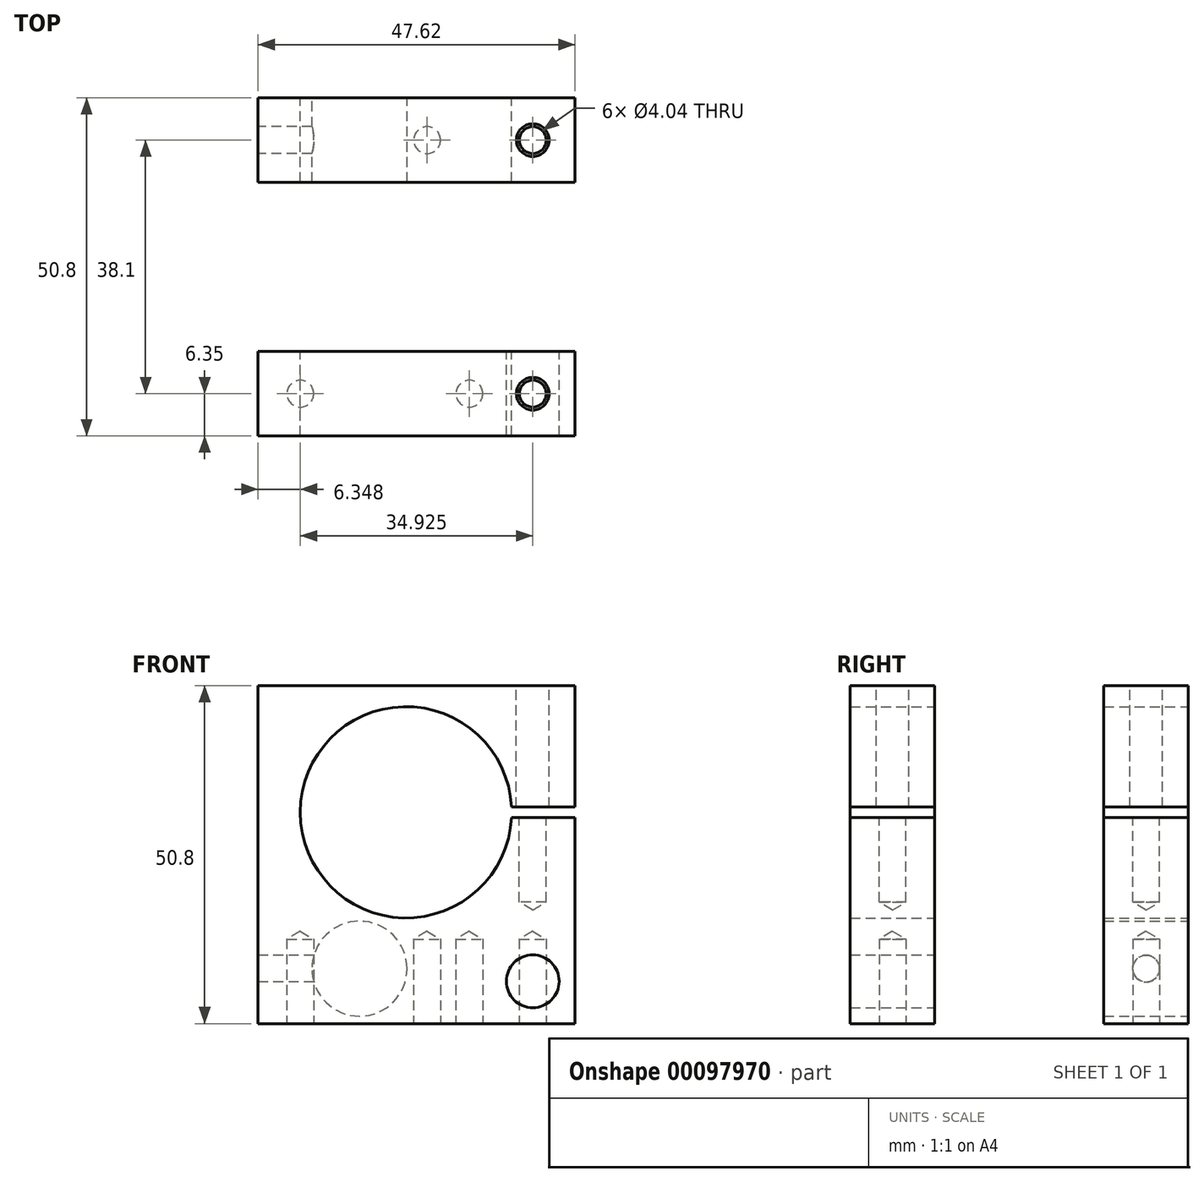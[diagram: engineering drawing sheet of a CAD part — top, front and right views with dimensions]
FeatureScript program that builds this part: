
annotation { "Feature Type Name" : "Feature", "Feature Type Description" : "" }
export const myFeature = defineFeature(function(context is Context, id is Id, definition is map)
    precondition{}
    {
        {
            var Q0;
            Q0=qCreatedBy(makeId("Front.planeOp"),FACE);
            var sketch = newSketch(context, id + "F0", { "sketchPlane" : qUnion([Q0])});
            skLineSegment(sketch, "E0.bottom", {"start": v(23.81, -25.4) * mm, "end": v(-23.81, -25.4) * mm});
            skLineSegment(sketch, "E0.top", {"start": v(23.81, 25.4) * mm, "end": v(-23.81, 25.4) * mm});
            skLineSegment(sketch, "E0.left", {"start": v(23.81, -25.4) * mm, "end": v(23.81, 25.4) * mm});
            skLineSegment(sketch, "E0.right", {"start": v(-23.81, -25.4) * mm, "end": v(-23.81, 25.4) * mm});
            skPoint(sketch, "E0.middle", {"position": v(0, 0) * mm});
            skLineSegment(sketch, "E1", {"start": v(-1.59, 25.4) * mm, "end": v(-1.59, -25.4) * mm, "construction": true});
            skLineSegment(sketch, "E2", {"start": v(-23.81, 6.35) * mm, "end": v(23.81, 6.35) * mm, "construction": true});
            skArc(sketch, "E3", {"start": v(14.27, 7.14) * mm, "mid": v(-17.46, 6.35) * mm, "end": v(14.27, 5.56) * mm});
            skLineSegment(sketch, "E4", {"start": v(-23.81, -17.15) * mm, "end": v(23.81, -17.14) * mm, "construction": true});
            skLineSegment(sketch, "E5", {"start": v(-8.57, -17.15) * mm, "end": v(-8.57, -25.4) * mm, "construction": true});
            skCircle(sketch, "E6", {"center": v(-8.57, -17.15) * mm, "radius": 7.14 * mm});
            skLineSegment(sketch, "E7", {"start": v(-23.81, 7.14) * mm, "end": v(23.81, 7.14) * mm, "construction": true});
            skLineSegment(sketch, "E8", {"start": v(-23.81, 5.56) * mm, "end": v(23.81, 5.56) * mm, "construction": true});
            skLineSegment(sketch, "E9", {"start": v(14.27, 7.14) * mm, "end": v(23.81, 7.14) * mm});
            skLineSegment(sketch, "E10", {"start": v(14.27, 5.56) * mm, "end": v(23.81, 5.56) * mm});
            skSolve(sketch);
        }
        {
            var Q0;
            {var subQ3=sQuery(id+"F0.wireOp",EDGE,"E0.bottom");Q0=makeQuery(id+"F0.imprint","IMPRINT",FACE,{"disambiguationData":[TD([[makeQuery(id+"F0.imprint","IMPRINT",EDGE,{"derivedFrom":subQ3}),-1.0]])]});}
            extrude(context, id + "F1", {"entities" : qUnion([Q0]), "depth" : 12.7 * mm});
        }
        {
            var Q0;
            Q0=makeQuery(id+"F1.opExtrude","SWEPT_FACE",FACE,{"disambiguationData":[OSD([sQuery(id+"F0.wireOp",EDGE,"E0.right")])]});
            var sketch = newSketch(context, id + "F2", { "sketchPlane" : qUnion([Q0])});
            skLineSegment(sketch, "E11.0.0", {"start": v(0, 25.4) * mm, "end": v(0, -25.4) * mm});
            skLineSegment(sketch, "E11.0.1", {"start": v(0, -25.4) * mm, "end": v(12.7, -25.4) * mm});
            skLineSegment(sketch, "E11.0.2", {"start": v(12.7, -25.4) * mm, "end": v(12.7, 25.4) * mm});
            skLineSegment(sketch, "E11.0.3", {"start": v(12.7, 25.4) * mm, "end": v(0, 25.4) * mm});
            skPoint(sketch, "E12.0", {"position": v(0, -17.14) * mm});
            skLineSegment(sketch, "E13", {"start": v(0, -17.14) * mm, "end": v(12.7, -17.14) * mm, "construction": true});
            skPoint(sketch, "E14", {"position": v(6.35, -17.14) * mm});
            skSolve(sketch);
        }
        {
            var Q0;
            Q0=sQuery(id+"F2.wireOp",VERTEX,"E14");
            var Q1;
            Q1=makeQuery(id+"F1.opExtrude","SWEPT_BODY",BODY,{"disambiguationData":[OSD([sQuery(id+"F0.wireOp",EDGE,"E0.bottom"),sQuery(id+"F0.wireOp",EDGE,"E0.top"),sQuery(id+"F0.wireOp",EDGE,"E0.left"),sQuery(id+"F0.wireOp",EDGE,"E0.right"),sQuery(id+"F0.wireOp",EDGE,"E3"),sQuery(id+"F0.wireOp",EDGE,"E6"),sQuery(id+"F0.wireOp",EDGE,"E9"),sQuery(id+"F0.wireOp",EDGE,"E10")])]});
            hole(context, id + "F3", {"style" : HoleStyle.SIMPLE, "endStyle" : HoleEndStyle.BLIND, "standardTappedOrClearance" : lookupTablePath({ "standard" : "ANSI", "engagement" : "75%", "pitch" : "32 tpi", "size" : "#10", "type" : "Tapped" }), "standardBlindInLast" : lookupTablePath({ "standard" : "ANSI", "engagement" : "75%", "pitch" : "32 tpi", "size" : "#10", "type" : "Tapped" }), "holeDiameter" : 4.04 * mm, "holeDepth" : 9.52 * mm, "locations" : qUnion([Q0]), "scope" : qUnion([Q1]), "majorDiameter" : 4.83 * mm});
        }
        {
            var Q0;
            Q0=makeQuery(id+"F1.opExtrude","SWEPT_FACE",FACE,{"disambiguationData":[OSD([sQuery(id+"F0.wireOp",EDGE,"E0.bottom")])]});
            var sketch = newSketch(context, id + "F4", { "sketchPlane" : qUnion([Q0])});
            skLineSegment(sketch, "E15", {"start": v(17.46, 12.7) * mm, "end": v(17.46, 0) * mm, "construction": true});
            skLineSegment(sketch, "E16", {"start": v(1.59, 12.7) * mm, "end": v(1.59, 0) * mm, "construction": true});
            skPoint(sketch, "E17", {"position": v(1.59, 6.35) * mm});
            skPoint(sketch, "E18", {"position": v(17.46, 6.35) * mm});
            skSolve(sketch);
        }
        {
            var Q0;
            Q0=sQuery(id+"F4.wireOp",VERTEX,"E17");
            var Q1;
            Q1=sQuery(id+"F4.wireOp",VERTEX,"E18");
            var Q2;
            Q2=makeQuery(id+"F1.opExtrude","SWEPT_BODY",BODY,{"disambiguationData":[OSD([sQuery(id+"F0.wireOp",EDGE,"E0.bottom"),sQuery(id+"F0.wireOp",EDGE,"E0.top"),sQuery(id+"F0.wireOp",EDGE,"E0.left"),sQuery(id+"F0.wireOp",EDGE,"E0.right"),sQuery(id+"F0.wireOp",EDGE,"E3"),sQuery(id+"F0.wireOp",EDGE,"E6"),sQuery(id+"F0.wireOp",EDGE,"E9"),sQuery(id+"F0.wireOp",EDGE,"E10")])]});
            hole(context, id + "F5", {"style" : HoleStyle.SIMPLE, "endStyle" : HoleEndStyle.BLIND, "standardTappedOrClearance" : lookupTablePath({ "standard" : "ANSI", "engagement" : "75%", "pitch" : "32 tpi", "size" : "#10", "type" : "Tapped" }), "standardBlindInLast" : lookupTablePath({ "standard" : "ANSI", "engagement" : "75%", "pitch" : "32 tpi", "size" : "#10", "type" : "Tapped" }), "holeDiameter" : 4.04 * mm, "holeDepth" : 12.7 * mm, "locations" : qUnion([Q0, Q1]), "scope" : qUnion([Q2]), "majorDiameter" : 4.83 * mm});
        }
        {
            var Q0;
            Q0=makeQuery(id+"F1.opExtrude","SWEPT_FACE",FACE,{"disambiguationData":[OSD([sQuery(id+"F0.wireOp",EDGE,"E10")])]});
            var sketch = newSketch(context, id + "F6", { "sketchPlane" : qUnion([Q0])});
            skLineSegment(sketch, "E19.0", {"start": v(14.27, -12.7) * mm, "end": v(23.81, -12.7) * mm, "construction": true});
            skLineSegment(sketch, "E20.0", {"start": v(23.81, -12.7) * mm, "end": v(23.81, 0) * mm, "construction": true});
            skLineSegment(sketch, "E21", {"start": v(17.46, 0) * mm, "end": v(17.46, -12.7) * mm, "construction": true});
            skPoint(sketch, "E22", {"position": v(17.46, -6.35) * mm});
            skSolve(sketch);
        }
        {
            var Q0;
            Q0=sQuery(id+"F6.wireOp",VERTEX,"E22");
            var Q1;
            Q1=makeQuery(id+"F1.opExtrude","SWEPT_BODY",BODY,{"disambiguationData":[OSD([sQuery(id+"F0.wireOp",EDGE,"E0.bottom"),sQuery(id+"F0.wireOp",EDGE,"E0.top"),sQuery(id+"F0.wireOp",EDGE,"E0.left"),sQuery(id+"F0.wireOp",EDGE,"E0.right"),sQuery(id+"F0.wireOp",EDGE,"E3"),sQuery(id+"F0.wireOp",EDGE,"E6"),sQuery(id+"F0.wireOp",EDGE,"E9"),sQuery(id+"F0.wireOp",EDGE,"E10")])]});
            hole(context, id + "F7", {"style" : HoleStyle.SIMPLE, "endStyle" : HoleEndStyle.BLIND, "standardTappedOrClearance" : lookupTablePath({ "standard" : "ANSI", "engagement" : "75%", "pitch" : "32 tpi", "size" : "#10", "type" : "Tapped" }), "standardBlindInLast" : lookupTablePath({ "standard" : "ANSI", "engagement" : "75%", "pitch" : "32 tpi", "size" : "#10", "type" : "Tapped" }), "holeDiameter" : 4.04 * mm, "holeDepth" : 12.7 * mm, "locations" : qUnion([Q0]), "scope" : qUnion([Q1]), "majorDiameter" : 4.83 * mm});
        }
        {
            var Q0;
            Q0=makeQuery(id+"F1.opExtrude","SWEPT_FACE",FACE,{"disambiguationData":[OSD([sQuery(id+"F0.wireOp",EDGE,"E0.top")])]});
            var sketch = newSketch(context, id + "F8", { "sketchPlane" : qUnion([Q0])});
            skPoint(sketch, "E23.0", {"position": v(17.46, -6.35) * mm});
            skSolve(sketch);
        }
        {
            var Q0;
            Q0=sQuery(id+"F8.wireOp",VERTEX,"E23.0");
            var Q1;
            Q1=makeQuery(id+"F1.opExtrude","SWEPT_BODY",BODY,{"disambiguationData":[OSD([sQuery(id+"F0.wireOp",EDGE,"E0.bottom"),sQuery(id+"F0.wireOp",EDGE,"E0.top"),sQuery(id+"F0.wireOp",EDGE,"E0.left"),sQuery(id+"F0.wireOp",EDGE,"E0.right"),sQuery(id+"F0.wireOp",EDGE,"E3"),sQuery(id+"F0.wireOp",EDGE,"E6"),sQuery(id+"F0.wireOp",EDGE,"E9"),sQuery(id+"F0.wireOp",EDGE,"E10")])]});
            hole(context, id + "F9", {"style" : HoleStyle.SIMPLE, "endStyle" : HoleEndStyle.BLIND, "standardTappedOrClearance" : lookupTablePath({ "standard" : "ANSI", "size" : "#10 (0.2)", "type" : "Drilled" }), "standardBlindInLast" : lookupTablePath({ "standard" : "ANSI", "size" : "#10", "type" : "Drilled" }), "holeDiameter" : 4.9 * mm, "holeDepth" : 18.29 * mm, "locations" : qUnion([Q0]), "scope" : qUnion([Q1])});
        }
        {
            var Q0;
            Q0=makeQuery(id+"F1.opExtrude","CAP_FACE",FACE,{"disambiguationData":[OSD([sQuery(id+"F0.wireOp",EDGE,"E0.bottom"),sQuery(id+"F0.wireOp",EDGE,"E0.top"),sQuery(id+"F0.wireOp",EDGE,"E0.left"),sQuery(id+"F0.wireOp",EDGE,"E0.right"),sQuery(id+"F0.wireOp",EDGE,"E3"),sQuery(id+"F0.wireOp",EDGE,"E6"),sQuery(id+"F0.wireOp",EDGE,"E9"),sQuery(id+"F0.wireOp",EDGE,"E10")])],"isStart":false});
            cPlane(context, id + "F10", {"entities" : qUnion([Q0]), "cplaneType" : CPlaneType.OFFSET, "offset" : 25.4 * mm, "width" : 152.4 * mm, "height" : 152.4 * mm});
        }
        {
            var Q0;
            Q0=qCreatedBy(id+"F10.planeOp",FACE);
            var sketch = newSketch(context, id + "F11", { "sketchPlane" : qUnion([Q0])});
            skLineSegment(sketch, "E24.0.0", {"start": v(-23.81, -25.4) * mm, "end": v(23.81, -25.4) * mm});
            skLineSegment(sketch, "E24.0.1", {"start": v(23.81, -25.4) * mm, "end": v(23.81, 5.56) * mm});
            skLineSegment(sketch, "E24.0.2", {"start": v(23.81, 5.56) * mm, "end": v(14.27, 5.56) * mm});
            skArc(sketch, "E24.0.3", {"start": v(14.27, 5.56) * mm, "mid": v(-17.46, 6.35) * mm, "end": v(14.27, 7.14) * mm});
            skLineSegment(sketch, "E24.0.4", {"start": v(14.27, 7.14) * mm, "end": v(23.81, 7.14) * mm});
            skLineSegment(sketch, "E24.0.5", {"start": v(23.81, 7.14) * mm, "end": v(23.81, 25.4) * mm});
            skLineSegment(sketch, "E24.0.6", {"start": v(23.81, 25.4) * mm, "end": v(-23.81, 25.4) * mm});
            skLineSegment(sketch, "E24.0.7", {"start": v(-23.81, 25.4) * mm, "end": v(-23.81, -25.4) * mm});
            skLineSegment(sketch, "E25", {"start": v(-23.81, -19.05) * mm, "end": v(23.81, -19.05) * mm, "construction": true});
            skLineSegment(sketch, "E26", {"start": v(17.46, 25.4) * mm, "end": v(17.46, -25.4) * mm, "construction": true});
            skCircle(sketch, "E27", {"center": v(17.46, -19.05) * mm, "radius": 3.96 * mm});
            skSolve(sketch);
        }
        {
            var Q0;
            Q0=makeQuery(id+"F11.imprint","IMPRINT",FACE,{"disambiguationData":[TD([[makeQuery(id+"F11.imprint","IMPRINT",EDGE,{"derivedFrom":sQuery(id+"F11.wireOp",EDGE,"E24.0.0")}),1.0]])]});
            extrude(context, id + "F12", {"entities" : qUnion([Q0]), "depth" : 12.7 * mm});
        }
        {
            var Q0;
            Q0=makeQuery(id+"F12.opExtrude","SWEPT_FACE",FACE,{"disambiguationData":[OSD([sQuery(id+"F11.wireOp",EDGE,"E24.0.2")])]});
            var sketch = newSketch(context, id + "F13", { "sketchPlane" : qUnion([Q0])});
            skLineSegment(sketch, "E28.0", {"start": v(23.81, -50.8) * mm, "end": v(23.81, -38.1) * mm, "construction": true});
            skLineSegment(sketch, "E29.0", {"start": v(23.81, -50.8) * mm, "end": v(14.27, -50.8) * mm, "construction": true});
            skLineSegment(sketch, "E30", {"start": v(17.46, -38.1) * mm, "end": v(17.46, -50.8) * mm, "construction": true});
            skPoint(sketch, "E31", {"position": v(17.46, -44.45) * mm});
            skSolve(sketch);
        }
        {
            var Q0;
            Q0=sQuery(id+"F13.wireOp",VERTEX,"E31");
            var Q1;
            Q1=makeQuery(id+"F12.opExtrude","SWEPT_BODY",BODY,{"disambiguationData":[OSD([sQuery(id+"F11.wireOp",EDGE,"E24.0.0"),sQuery(id+"F11.wireOp",EDGE,"E24.0.1"),sQuery(id+"F11.wireOp",EDGE,"E24.0.2"),sQuery(id+"F11.wireOp",EDGE,"E24.0.3"),sQuery(id+"F11.wireOp",EDGE,"E24.0.4"),sQuery(id+"F11.wireOp",EDGE,"E24.0.5"),sQuery(id+"F11.wireOp",EDGE,"E24.0.6"),sQuery(id+"F11.wireOp",EDGE,"E24.0.7"),sQuery(id+"F11.wireOp",EDGE,"E27")])]});
            hole(context, id + "F14", {"style" : HoleStyle.SIMPLE, "endStyle" : HoleEndStyle.BLIND, "standardTappedOrClearance" : lookupTablePath({ "standard" : "ANSI", "engagement" : "75%", "pitch" : "32 tpi", "size" : "#10", "type" : "Tapped" }), "standardBlindInLast" : lookupTablePath({ "standard" : "ANSI", "engagement" : "75%", "pitch" : "32 tpi", "size" : "#10", "type" : "Tapped" }), "holeDiameter" : 4.04 * mm, "holeDepth" : 12.7 * mm, "locations" : qUnion([Q0]), "scope" : qUnion([Q1]), "majorDiameter" : 4.83 * mm});
        }
        {
            var Q0;
            Q0=makeQuery(id+"F12.opExtrude","SWEPT_FACE",FACE,{"disambiguationData":[OSD([sQuery(id+"F11.wireOp",EDGE,"E24.0.6")])]});
            var sketch = newSketch(context, id + "F15", { "sketchPlane" : qUnion([Q0])});
            skPoint(sketch, "E32.0", {"position": v(17.46, -44.45) * mm});
            skSolve(sketch);
        }
        {
            var Q0;
            Q0=sQuery(id+"F15.wireOp",VERTEX,"E32.0");
            var Q1;
            Q1=makeQuery(id+"F12.opExtrude","SWEPT_BODY",BODY,{"disambiguationData":[OSD([sQuery(id+"F11.wireOp",EDGE,"E24.0.0"),sQuery(id+"F11.wireOp",EDGE,"E24.0.1"),sQuery(id+"F11.wireOp",EDGE,"E24.0.2"),sQuery(id+"F11.wireOp",EDGE,"E24.0.3"),sQuery(id+"F11.wireOp",EDGE,"E24.0.4"),sQuery(id+"F11.wireOp",EDGE,"E24.0.5"),sQuery(id+"F11.wireOp",EDGE,"E24.0.6"),sQuery(id+"F11.wireOp",EDGE,"E24.0.7"),sQuery(id+"F11.wireOp",EDGE,"E27")])]});
            hole(context, id + "F16", {"style" : HoleStyle.SIMPLE, "endStyle" : HoleEndStyle.BLIND, "standardTappedOrClearance" : lookupTablePath({ "standard" : "ANSI", "size" : "#10 (0.2)", "type" : "Drilled" }), "standardBlindInLast" : lookupTablePath({ "standard" : "ANSI", "size" : "#10", "type" : "Drilled" }), "holeDiameter" : 4.9 * mm, "holeDepth" : 18.29 * mm, "locations" : qUnion([Q0]), "scope" : qUnion([Q1])});
        }
        {
            var Q0;
            Q0=makeQuery(id+"F12.opExtrude","SWEPT_FACE",FACE,{"disambiguationData":[OSD([sQuery(id+"F11.wireOp",EDGE,"E24.0.0")])]});
            var sketch = newSketch(context, id + "F17", { "sketchPlane" : qUnion([Q0])});
            skLineSegment(sketch, "E33", {"start": v(7.94, 50.8) * mm, "end": v(7.94, 38.1) * mm, "construction": true});
            skLineSegment(sketch, "E34", {"start": v(-17.46, 50.8) * mm, "end": v(-17.46, 38.1) * mm, "construction": true});
            skPoint(sketch, "E35", {"position": v(-17.46, 44.45) * mm});
            skPoint(sketch, "E36", {"position": v(7.94, 44.45) * mm});
            skSolve(sketch);
        }
        {
            var Q0;
            Q0=sQuery(id+"F17.wireOp",VERTEX,"E35");
            var Q1;
            Q1=sQuery(id+"F17.wireOp",VERTEX,"E36");
            var Q2;
            Q2=makeQuery(id+"F12.opExtrude","SWEPT_BODY",BODY,{"disambiguationData":[OSD([sQuery(id+"F11.wireOp",EDGE,"E24.0.0"),sQuery(id+"F11.wireOp",EDGE,"E24.0.1"),sQuery(id+"F11.wireOp",EDGE,"E24.0.2"),sQuery(id+"F11.wireOp",EDGE,"E24.0.3"),sQuery(id+"F11.wireOp",EDGE,"E24.0.4"),sQuery(id+"F11.wireOp",EDGE,"E24.0.5"),sQuery(id+"F11.wireOp",EDGE,"E24.0.6"),sQuery(id+"F11.wireOp",EDGE,"E24.0.7"),sQuery(id+"F11.wireOp",EDGE,"E27")])]});
            hole(context, id + "F18", {"style" : HoleStyle.SIMPLE, "endStyle" : HoleEndStyle.BLIND, "standardTappedOrClearance" : lookupTablePath({ "standard" : "ANSI", "engagement" : "75%", "pitch" : "32 tpi", "size" : "#10", "type" : "Tapped" }), "standardBlindInLast" : lookupTablePath({ "standard" : "ANSI", "engagement" : "75%", "pitch" : "32 tpi", "size" : "#10", "type" : "Tapped" }), "holeDiameter" : 4.04 * mm, "holeDepth" : 12.7 * mm, "locations" : qUnion([Q0, Q1]), "scope" : qUnion([Q2]), "majorDiameter" : 4.83 * mm});
        }
    });
